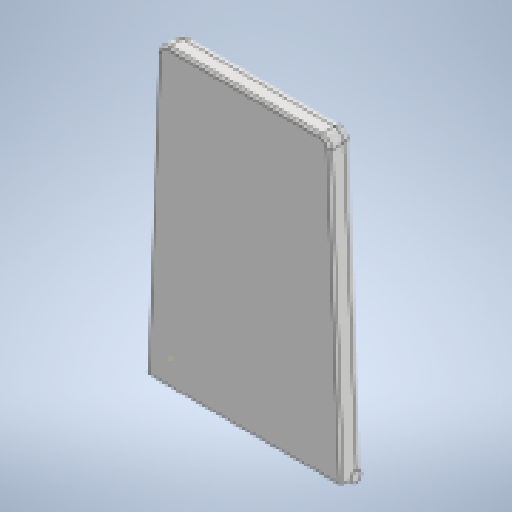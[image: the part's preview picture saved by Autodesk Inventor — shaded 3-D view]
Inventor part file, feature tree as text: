
AUTODESK INVENTOR PART (.ipt)
format: ipt  version: 2023 (Build 270158000, 158)  size: 185,856 bytes
history: native  units: in
note: dims shown in document units (in); Inventor stores cm internally (conversion verified against a paired STEP export)
features: sketch x4, extrude x3, fillet x2
ambient origin geometry x8: Origin, YZ Plane, XZ Plane, XY Plane, X Axis, Y Axis, Z Axis, Center Point
bodies: Solid1 (feature_tree)
feature tree (9):
  extrude  "Extrusion1"  Depth=0.9843in
  fillet  "Fillet1"  Radius=13.7795in
  fillet  "Fillet2"  Radius=15.748in
  sketch  "Sketch2"  dims[d4=6.8898in d5=1.9685in d6=0.0in]
  extrude  "Extrusion2"  Depth=1.9685in TaperAngle=0.0deg
  extrude  "Extrusion3"  Depth=0.1969in
  sketch  "Sketch1"  dims[d0=23.622in d1=0.9843in d2=13.7795in d3=15.748in]
  sketch  "Sketch3"  dims[d7=0.7874in d8=0.1969in]
  sketch  "Sketch4"  dims[d9=0.876in d10=15.748in d11=0.0in d12=0.876in d13=9.8425in d14=1.1811in d15=0.0in d16=4.9213in]
